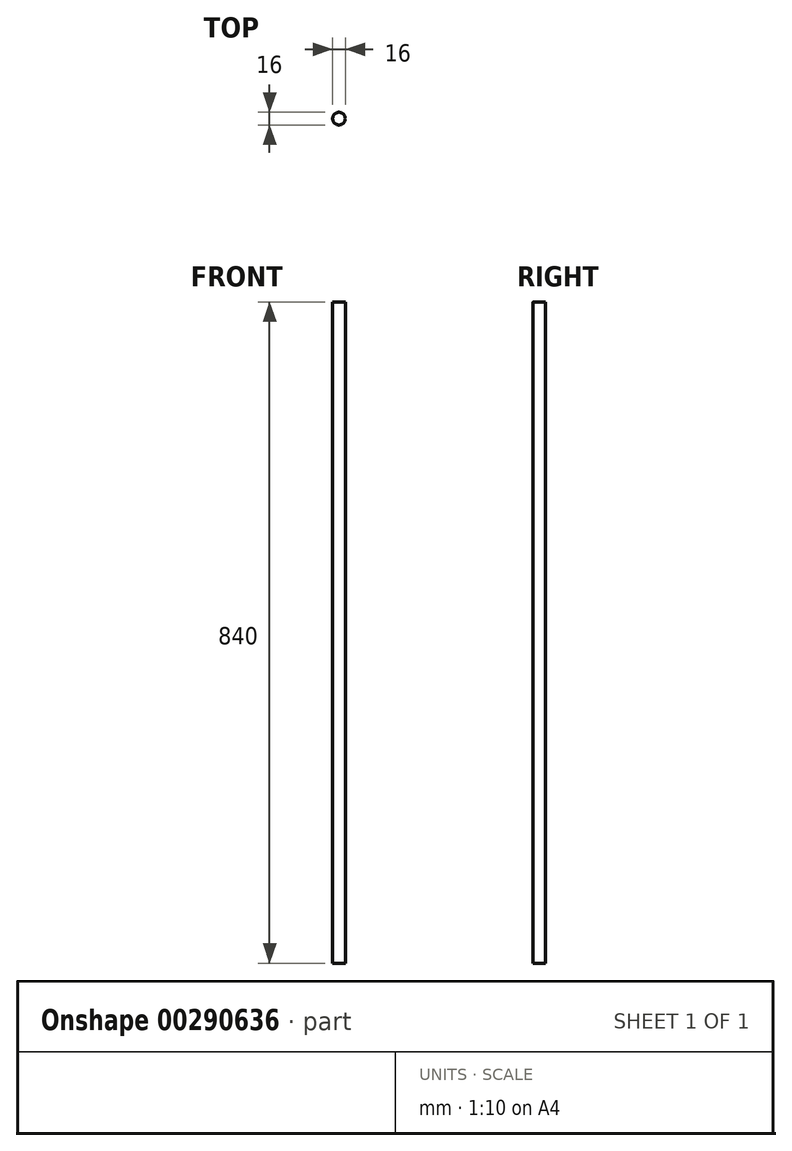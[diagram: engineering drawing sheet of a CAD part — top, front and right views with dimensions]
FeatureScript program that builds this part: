
annotation { "Feature Type Name" : "Feature", "Feature Type Description" : "" }
export const myFeature = defineFeature(function(context is Context, id is Id, definition is map)
    precondition{}
    {
        {
            var Q0;
            Q0=qCreatedBy(makeId("Top.planeOp"),FACE);
            var sketch = newSketch(context, id + "F0", { "sketchPlane" : qUnion([Q0])});
            skCircle(sketch, "E0", {"center": v(0, 0) * mm, "radius": 8 * mm});
            skSolve(sketch);
        }
        {
            var Q0;
            Q0=qSketchRegion(id+"F0",true);
            extrude(context, id + "F1", {"entities" : qUnion([Q0]), "depth" : 840 * mm});
        }
    });
